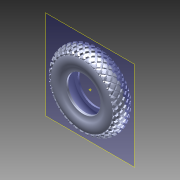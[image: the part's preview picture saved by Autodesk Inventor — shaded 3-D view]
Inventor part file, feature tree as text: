
AUTODESK INVENTOR PART (.ipt)
format: ipt  version: 2013 (Build 170138000, 138)  size: 11,076,096 bytes
history: native  units: in
note: dims shown in document units (in); Inventor stores cm internally (conversion verified against a paired STEP export)
features: pattern_circular x1, imported_body x1, plane x1, other x1
ambient origin geometry x8: Origin, YZ Plane, XZ Plane, XY Plane, X Axis, Y Axis, Z Axis, Center Point
feature tree (4):
  pattern_circular  "CirPattern1"
  imported_body  "Base1"
  plane  "Work Plane1"
  other  "Work Point1"
